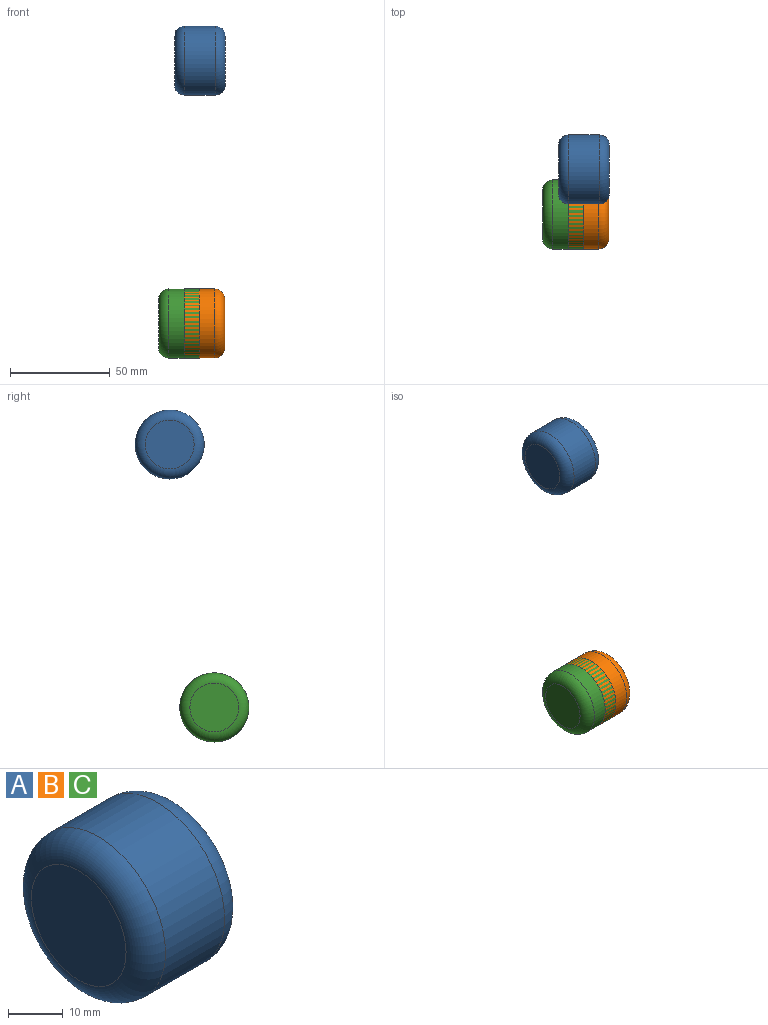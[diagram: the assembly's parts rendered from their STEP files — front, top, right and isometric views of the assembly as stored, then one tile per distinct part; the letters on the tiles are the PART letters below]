
ASSEMBLY  parts=3 mates=1
PART A: 5 faces, bbox 25.4x37.4x37.4 mm
  f0: cylinder r=17.28mm len=34.56mm, axis (-1,0,0), area 1654.7mm2, adj f3,f4
  f1: plane 24.4x24.4mm, normal (1,0,0), area 467.6mm2, adj f4
  f2: plane 24.4x24.4mm, normal (-1,0,0), area 467.6mm2, adj f3
  f3: torus R=12.2mm, axis (1,0,0), area 773.8mm2, adj f0,f2
  f4: torus R=12.2mm, axis (1,0,0), area 773.8mm2, adj f0,f1
PART B: same geometry as A
PART C: same geometry as A
PLACE A t=(-14.1,-2.06,130.74)mm
PLACE B rot(axis=(-1,0,0),105.1deg) t=(-14.39,-24.37,-0.84)mm
PLACE C t=(-22.01,-24.37,-0.84)mm fixed
MATE revolute B.f0 <-> C.f0  axis (-1,0,0) through (-9.31,-24.37,-0.84)mm
